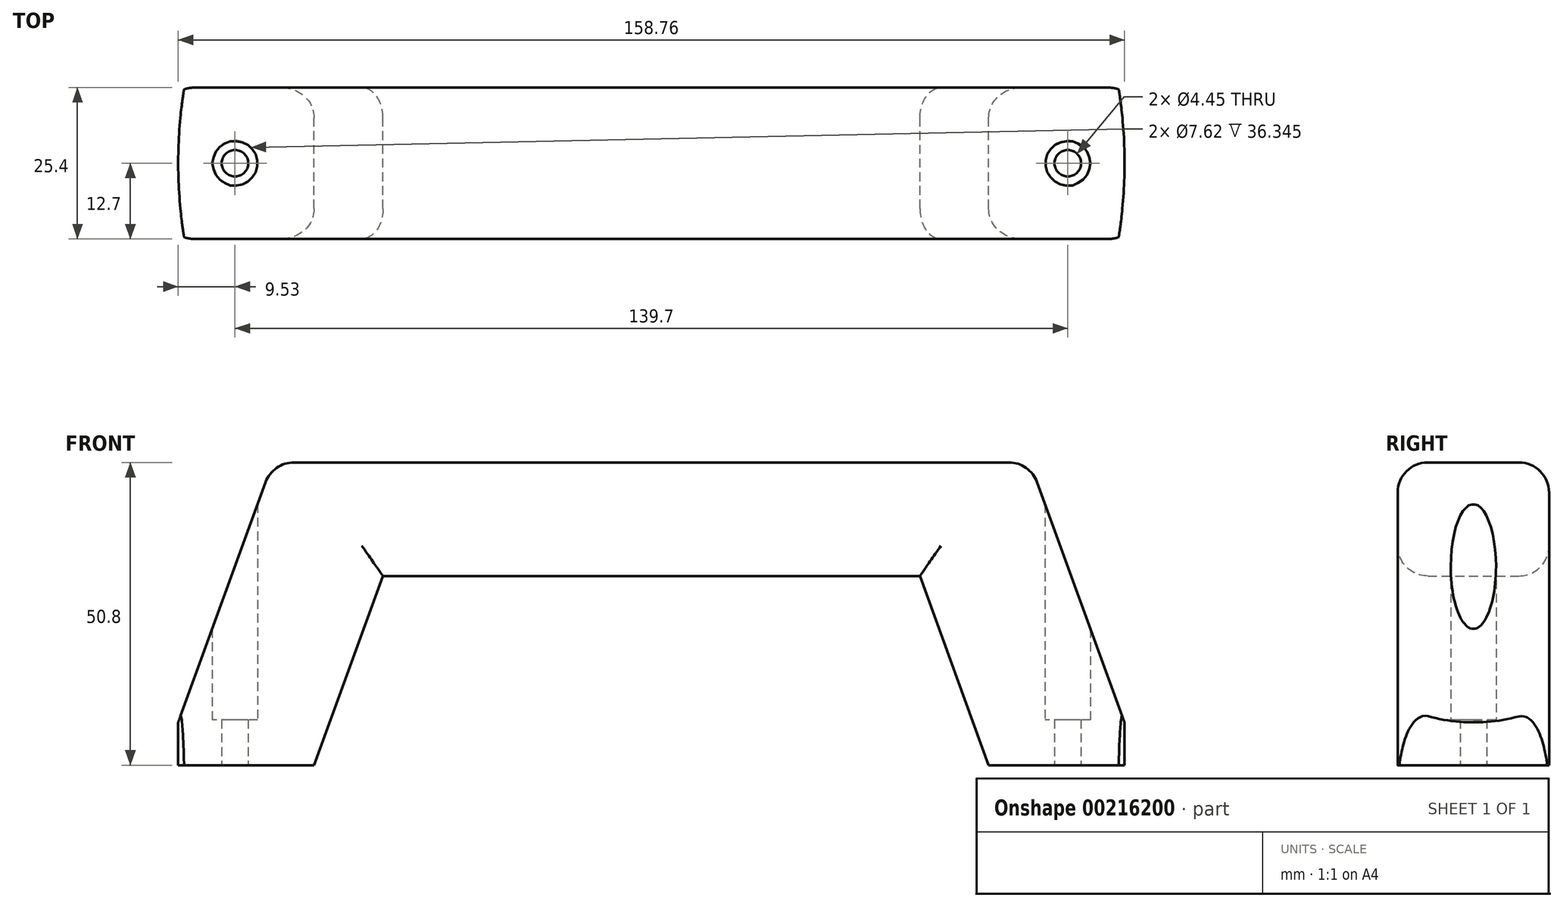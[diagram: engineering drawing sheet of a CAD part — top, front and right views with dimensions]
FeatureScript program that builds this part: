
annotation { "Feature Type Name" : "Feature", "Feature Type Description" : "" }
export const myFeature = defineFeature(function(context is Context, id is Id, definition is map)
    precondition{}
    {
        {
            var Q0;
            Q0=qCreatedBy(makeId("Front.planeOp"),FACE);
            var sketch = newSketch(context, id + "F0", { "sketchPlane" : qUnion([Q0])});
            skLineSegment(sketch, "E0", {"start": v(-81.99, 0) * mm, "end": v(-63.5, 50.8) * mm});
            skLineSegment(sketch, "E1", {"start": v(-63.5, 50.8) * mm, "end": v(63.5, 50.8) * mm});
            skLineSegment(sketch, "E2", {"start": v(63.5, 50.8) * mm, "end": v(81.99, 0) * mm});
            skLineSegment(sketch, "E3", {"start": v(81.99, 0) * mm, "end": v(56.59, 0) * mm});
            skLineSegment(sketch, "E4", {"start": v(56.59, 0) * mm, "end": v(45.03, 31.75) * mm});
            skLineSegment(sketch, "E5", {"start": v(45.03, 31.75) * mm, "end": v(-45.03, 31.75) * mm});
            skLineSegment(sketch, "E6", {"start": v(-45.03, 31.75) * mm, "end": v(-56.59, 0) * mm});
            skLineSegment(sketch, "E7", {"start": v(-56.59, 0) * mm, "end": v(-81.99, 0) * mm});
            skSolve(sketch);
        }
        {
            var Q0;
            Q0=makeQuery(id+"F0.imprint","IMPRINT",FACE,{"disambiguationData":[TD([[makeQuery(id+"F0.imprint","IMPRINT",EDGE,{"derivedFrom":sQuery(id+"F0.wireOp",EDGE,"E0")}),-1.0]])]});
            extrude(context, id + "F1", {"entities" : qUnion([Q0]), "depth" : 25.4 * mm});
        }
        {
            var Q0;
            Q0=makeQuery(id+"F1.opExtrude","SWEPT_FACE",FACE,{"disambiguationData":[OSD([sQuery(id+"F0.wireOp",EDGE,"E3")])]});
            var sketch = newSketch(context, id + "F2", { "sketchPlane" : qUnion([Q0])});
            skCircle(sketch, "E8", {"center": v(69.85, 12.7) * mm, "radius": 2.22 * mm});
            skPoint(sketch, "E8.centerSnap0", {"position": v(81.99, 12.7) * mm});
            skCircle(sketch, "E9", {"center": v(-69.85, 12.7) * mm, "radius": 2.22 * mm});
            skSolve(sketch);
        }
        {
            var Q0;
            Q0 = qSketchRegion(id + "F2", true);
            extrude(context, id + "F3", {"entities" : qUnion([Q0]), "operationType" : NewBodyOperationType.REMOVE, "endBound" : BoundingType.UP_TO_NEXT, "oppositeDirection" : true, "depth" : 25.4 * mm});
        }
        {
            var Q0;
            Q0=makeQuery(id+"F1.opExtrude","CAP_EDGE",EDGE,{"disambiguationData":[OSD([sQuery(id+"F0.wireOp",EDGE,"E0")])],"isStart":false});
            var Q1;
            Q1=makeQuery(id+"F1.opExtrude","CAP_EDGE",EDGE,{"disambiguationData":[OSD([sQuery(id+"F0.wireOp",EDGE,"E6")])],"isStart":false});
            var Q2;
            Q2=makeQuery(id+"F1.opExtrude","CAP_EDGE",EDGE,{"disambiguationData":[OSD([sQuery(id+"F0.wireOp",EDGE,"E5")])],"isStart":false});
            var Q3;
            Q3=makeQuery(id+"F1.opExtrude","CAP_EDGE",EDGE,{"disambiguationData":[OSD([sQuery(id+"F0.wireOp",EDGE,"E4")])],"isStart":false});
            var Q4;
            Q4=makeQuery(id+"F1.opExtrude","CAP_EDGE",EDGE,{"disambiguationData":[OSD([sQuery(id+"F0.wireOp",EDGE,"E2")])],"isStart":false});
            var Q5;
            Q5=makeQuery(id+"F1.opExtrude","CAP_EDGE",EDGE,{"disambiguationData":[OSD([sQuery(id+"F0.wireOp",EDGE,"E1")])],"isStart":false});
            var Q6;
            Q6=makeQuery(id+"F1.opExtrude","CAP_EDGE",EDGE,{"disambiguationData":[OSD([sQuery(id+"F0.wireOp",EDGE,"E2")])],"isStart":true});
            var Q7;
            Q7=makeQuery(id+"F1.opExtrude","CAP_EDGE",EDGE,{"disambiguationData":[OSD([sQuery(id+"F0.wireOp",EDGE,"E4")])],"isStart":true});
            var Q8;
            Q8=makeQuery(id+"F1.opExtrude","CAP_EDGE",EDGE,{"disambiguationData":[OSD([sQuery(id+"F0.wireOp",EDGE,"E5")])],"isStart":true});
            var Q9;
            Q9=makeQuery(id+"F1.opExtrude","CAP_EDGE",EDGE,{"disambiguationData":[OSD([sQuery(id+"F0.wireOp",EDGE,"E6")])],"isStart":true});
            var Q10;
            Q10=makeQuery(id+"F1.opExtrude","CAP_EDGE",EDGE,{"disambiguationData":[OSD([sQuery(id+"F0.wireOp",EDGE,"E0")])],"isStart":true});
            var Q11;
            Q11=makeQuery(id+"F1.opExtrude","CAP_EDGE",EDGE,{"disambiguationData":[OSD([sQuery(id+"F0.wireOp",EDGE,"E1")])],"isStart":true});
            var Q12;
            Q12=makeQuery(id+"F1.opExtrude","SWEPT_EDGE",EDGE,{"disambiguationData":[OSD([sQuery(id+"F0.wireOp",EDGE,"E0"),sQuery(id+"F0.wireOp",EDGE,"E1")])]});
            var Q13;
            Q13=makeQuery(id+"F1.opExtrude","SWEPT_EDGE",EDGE,{"disambiguationData":[OSD([sQuery(id+"F0.wireOp",EDGE,"E1"),sQuery(id+"F0.wireOp",EDGE,"E2")])]});
            fillet(context, id + "F4", {"entities" : qUnion([Q0, Q1, Q2, Q3, Q4, Q5, Q6, Q7, Q8, Q9, Q10, Q11, Q12, Q13]), "radius" : 5.08 * mm, "tangentPropagation" : true, "allowEdgeOverflow" : false});
        }
        {
            var Q0;
            Q0=qCreatedBy(makeId("Top.planeOp"),FACE);
            cPlane(context, id + "F5", {"entities" : qUnion([Q0]), "cplaneType" : CPlaneType.OFFSET, "offset" : 7.62 * mm, "width" : 152.4 * mm, "height" : 152.4 * mm});
        }
        {
            var Q0;
            Q0=qCreatedBy(id+"F5.planeOp",FACE);
            var sketch = newSketch(context, id + "F6", { "sketchPlane" : qUnion([Q0])});
            skCircle(sketch, "E10", {"center": v(-69.85, -12.7) * mm, "radius": 3.81 * mm});
            skCircle(sketch, "E11", {"center": v(69.85, -12.7) * mm, "radius": 3.81 * mm});
            skSolve(sketch);
        }
        {
            var Q0;
            Q0 = qSketchRegion(id + "F6", true);
            var Q1;
            Q1=makeQuery(id+"F1.opExtrude","SWEPT_FACE",FACE,{"disambiguationData":[OSD([sQuery(id+"F0.wireOp",EDGE,"E1")])]});
            extrude(context, id + "F7", {"entities" : qUnion([Q0]), "operationType" : NewBodyOperationType.REMOVE, "endBound" : BoundingType.UP_TO_SURFACE, "endBoundEntityFace" : qUnion([Q1]), "depth" : 25.4 * mm});
        }
        {
            var Q0;
            Q0=qCreatedBy(makeId("Top.planeOp"),FACE);
            var sketch = newSketch(context, id + "F8", { "sketchPlane" : qUnion([Q0])});
            skCircle(sketch, "E12", {"center": v(0, -12.66) * mm, "radius": 79.38 * mm});
            skCircle(sketch, "E13", {"center": v(0, -12.66) * mm, "radius": 88.7 * mm});
            skSolve(sketch);
        }
        {
            var Q0;
            Q0 = qSketchRegion(id + "F8", true);
            extrude(context, id + "F9", {"entities" : qUnion([Q0]), "operationType" : NewBodyOperationType.REMOVE, "depth" : 25.4 * mm});
        }
    });
